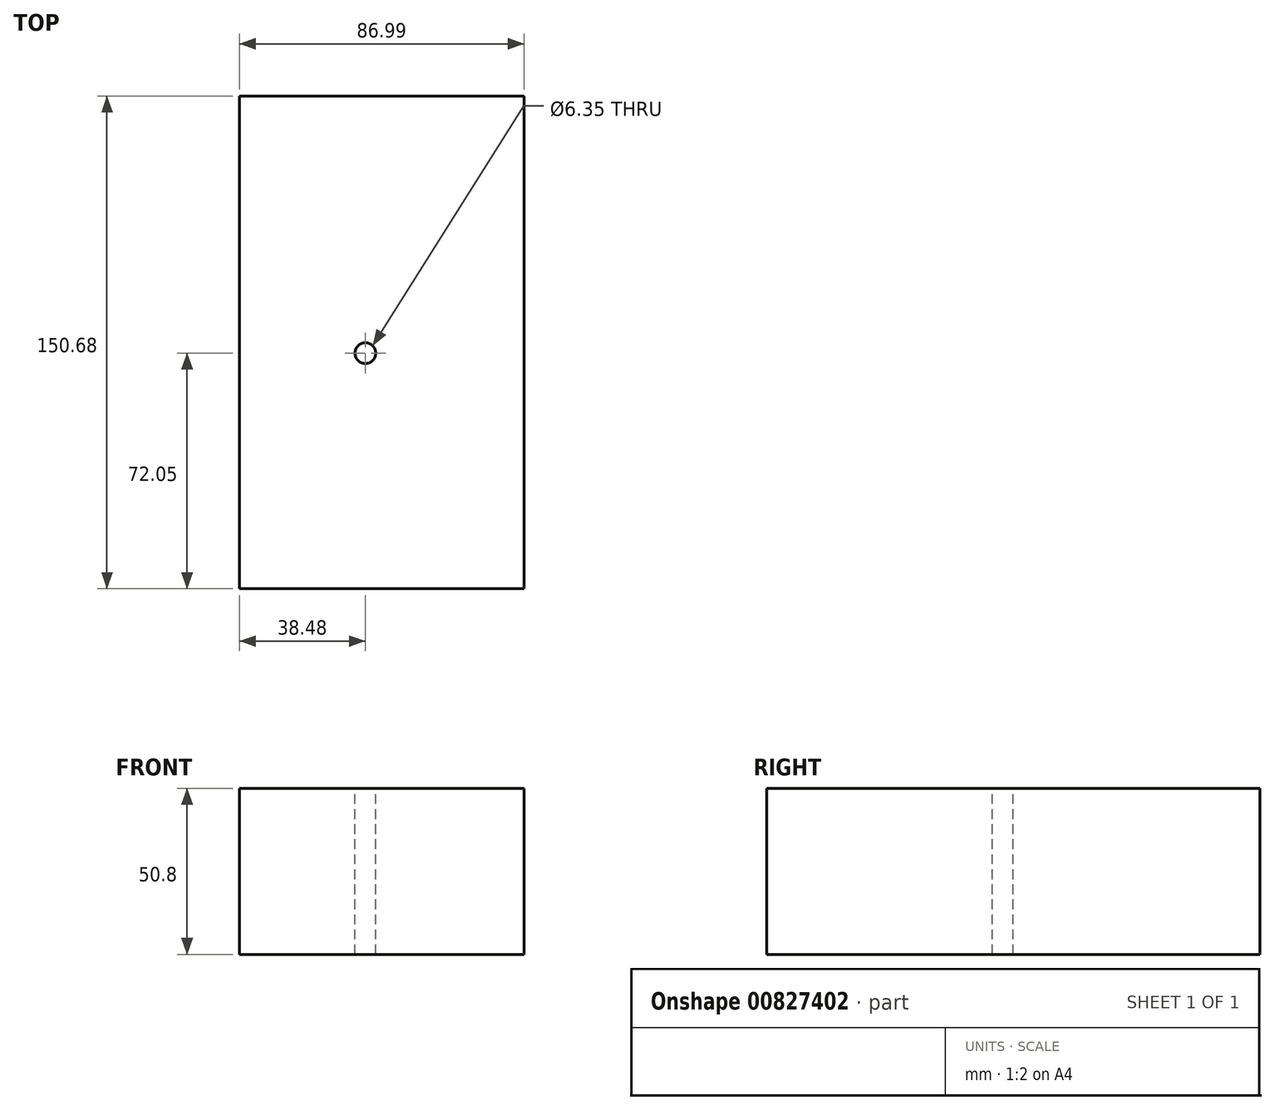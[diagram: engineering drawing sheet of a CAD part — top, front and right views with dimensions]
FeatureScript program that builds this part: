
annotation { "Feature Type Name" : "Feature", "Feature Type Description" : "" }
export const myFeature = defineFeature(function(context is Context, id is Id, definition is map)
    precondition{}
    {
        {
            var Q0;
            Q0=qCreatedBy(makeId("Top.planeOp"),FACE);
            var sketch = newSketch(context, id + "F0", { "sketchPlane" : qUnion([Q0])});
            skLineSegment(sketch, "E0.bottom", {"start": v(48.5, -46.65) * mm, "end": v(-38.48, -46.65) * mm});
            skLineSegment(sketch, "E0.top", {"start": v(48.5, 78.63) * mm, "end": v(-38.48, 78.63) * mm});
            skLineSegment(sketch, "E0.left", {"start": v(48.5, -46.65) * mm, "end": v(48.5, 78.63) * mm});
            skLineSegment(sketch, "E0.right", {"start": v(-38.48, -46.65) * mm, "end": v(-38.48, 78.63) * mm});
            skSolve(sketch);
        }
        {
            var Q0;
            Q0 = qSketchRegion(id + "F0", true);
            extrude(context, id + "F1", {"entities" : qUnion([Q0]), "depth" : 25.4 * mm, "offsetDistance" : 25.4 * mm});
        }
        {
            var Q0;
            Q0=makeQuery(id+"F1.opExtrude","SWEPT_FACE",FACE,{"disambiguationData":[OSD([sQuery(id+"F0.wireOp",EDGE,"E0.bottom")])]});
            extrude(context, id + "F2", {"entities" : qUnion([Q0]), "operationType" : NewBodyOperationType.ADD, "depth" : 25.4 * mm, "offsetDistance" : 25.4 * mm});
        }
        {
            var Q0;
            {var subQ0=sQuery(id+"F0.wireOp",EDGE,"E0.bottom");Q0=makeQuery(id+"F2.boolean.opBoolean","MERGE",FACE,{"derivedFrom":[makeQuery(id+"F1.opExtrude","CAP_FACE",FACE,{"disambiguationData":[OSD([subQ0,sQuery(id+"F0.wireOp",EDGE,"E0.top"),sQuery(id+"F0.wireOp",EDGE,"E0.left"),sQuery(id+"F0.wireOp",EDGE,"E0.right")])],"isStart":false}),makeQuery(id+"F2.opExtrude","SWEPT_FACE",FACE,{"disambiguationData":[OSD([subQ0]),TDD([makeQuery(id+"F1.opExtrude","CAP_EDGE",EDGE,{"disambiguationData":[OSD([subQ0])],"isStart":false})])]})]});}
            var sketch = newSketch(context, id + "F3", { "sketchPlane" : qUnion([Q0])});
            skCircle(sketch, "E1", {"center": v(0, 0) * mm, "radius": 38.59 * mm});
            skSolve(sketch);
        }
        {
            var Q0;
            Q0=sQuery(id+"F3.wireOp",VERTEX,"E1.center");
            var Q1;
            Q1=makeQuery(id+"F1.opExtrude","SWEPT_BODY",BODY,{"disambiguationData":[OSD([sQuery(id+"F0.wireOp",EDGE,"E0.bottom"),sQuery(id+"F0.wireOp",EDGE,"E0.top"),sQuery(id+"F0.wireOp",EDGE,"E0.left"),sQuery(id+"F0.wireOp",EDGE,"E0.right")])]});
            hole(context, id + "F4", {"style" : HoleStyle.SIMPLE, "endStyle" : HoleEndStyle.THROUGH, "holeDiameter" : 6.35 * mm, "majorDiameter" : 6.35 * mm, "isTappedThrough" : true, "tappedDepth" : 12.7 * mm, "tapClearance" : 3, "locations" : qUnion([Q0]), "scope" : qUnion([Q1])});
        }
        {
            var Q0;
            {var subQ0=sQuery(id+"F0.wireOp",EDGE,"E0.bottom");Q0=makeQuery(id+"F2.boolean.opBoolean","MERGE",FACE,{"derivedFrom":[makeQuery(id+"F1.opExtrude","CAP_FACE",FACE,{"disambiguationData":[OSD([subQ0,sQuery(id+"F0.wireOp",EDGE,"E0.top"),sQuery(id+"F0.wireOp",EDGE,"E0.left"),sQuery(id+"F0.wireOp",EDGE,"E0.right")])],"isStart":false}),makeQuery(id+"F2.opExtrude","SWEPT_FACE",FACE,{"disambiguationData":[OSD([subQ0]),TDD([makeQuery(id+"F1.opExtrude","CAP_EDGE",EDGE,{"disambiguationData":[OSD([subQ0])],"isStart":false})])]})]});}
            extrude(context, id + "F5", {"entities" : qUnion([Q0]), "operationType" : NewBodyOperationType.ADD, "depth" : 25.4 * mm, "offsetDistance" : 25.4 * mm});
        }
    });
